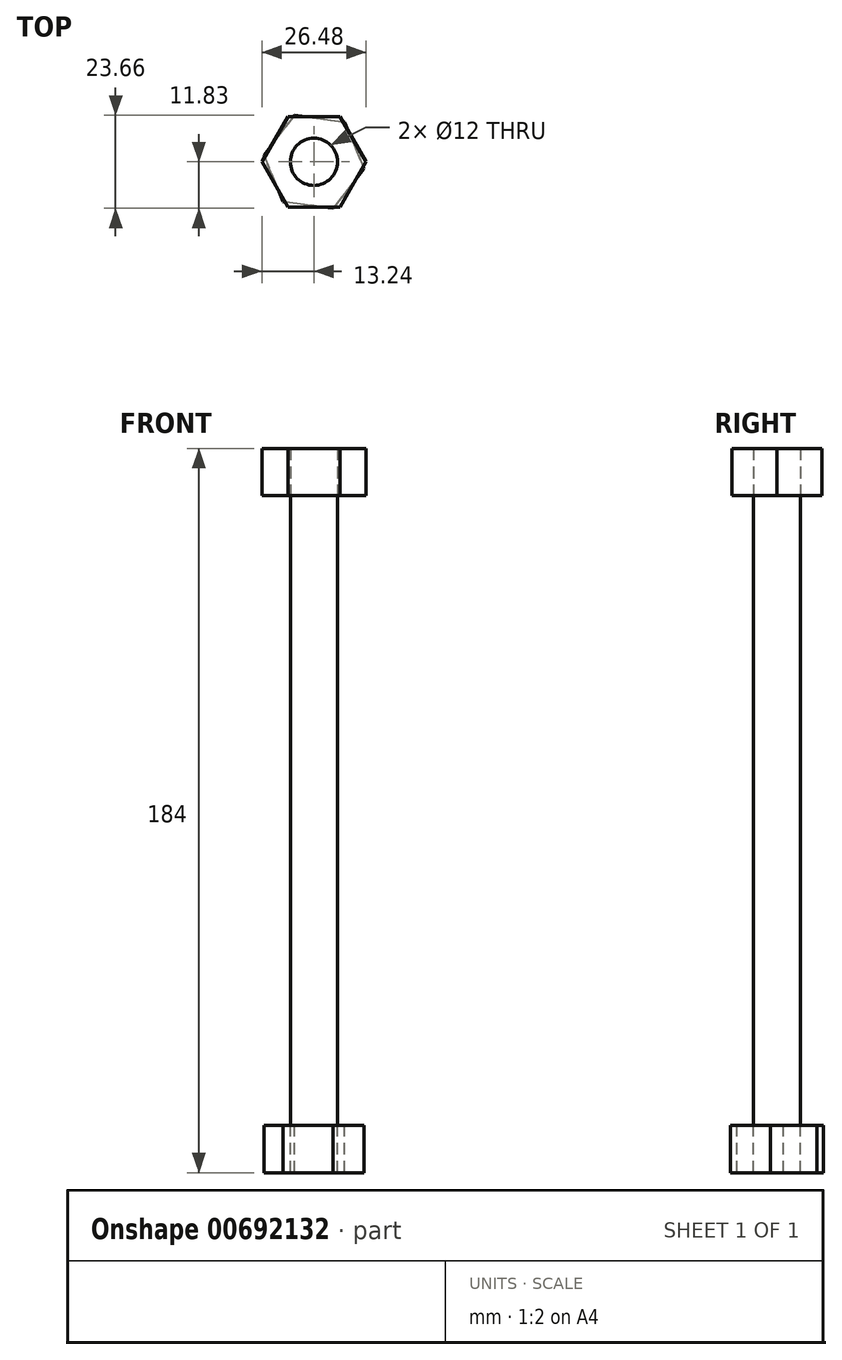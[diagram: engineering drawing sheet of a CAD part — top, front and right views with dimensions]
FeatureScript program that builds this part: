
annotation { "Feature Type Name" : "Feature", "Feature Type Description" : "" }
export const myFeature = defineFeature(function(context is Context, id is Id, definition is map)
    precondition{}
    {
        {
            var Q0;
            Q0=qCreatedBy(makeId("Top.planeOp"),FACE);
            var sketch = newSketch(context, id + "F0", { "sketchPlane" : qUnion([Q0])});
            skCircle(sketch, "E0", {"center": v(0, 0) * mm, "radius": 6 * mm});
            skCircle(sketch, "E1.cCircle", {"center": v(0, 0) * mm, "radius": 11.08 * mm, "construction": true});
            skLineSegment(sketch, "E1.0", {"start": v(-12.68, 1.69) * mm, "end": v(-4.88, 11.83) * mm});
            skLineSegment(sketch, "E1.1", {"start": v(-4.88, 11.83) * mm, "end": v(7.8, 10.14) * mm});
            skLineSegment(sketch, "E1.2", {"start": v(7.8, 10.14) * mm, "end": v(12.68, -1.69) * mm});
            skLineSegment(sketch, "E1.3", {"start": v(12.68, -1.69) * mm, "end": v(4.88, -11.83) * mm});
            skLineSegment(sketch, "E1.4", {"start": v(4.88, -11.83) * mm, "end": v(-7.8, -10.14) * mm});
            skLineSegment(sketch, "E1.5", {"start": v(-7.8, -10.14) * mm, "end": v(-12.68, 1.69) * mm});
            skPoint(sketch, "E1.0.midPoint", {"position": v(-8.78, 6.76) * mm});
            skSolve(sketch);
        }
        {
            var Q0;
            Q0=makeQuery(id+"F0.imprint","IMPRINT",FACE,{"disambiguationData":[TD([[makeQuery(id+"F0.imprint","IMPRINT",EDGE,{"derivedFrom":sQuery(id+"F0.wireOp",EDGE,"E0")}),1.0]])]});
            extrude(context, id + "F1", {"entities" : qUnion([Q0]), "depth" : 160 * mm, "offsetDistance" : 25 * mm});
        }
        {
            var Q0;
            Q0=qSketchRegion(id+"F0",true);
            extrude(context, id + "F2", {"entities" : qUnion([Q0]), "operationType" : NewBodyOperationType.ADD, "oppositeDirection" : true, "depth" : 12 * mm, "offsetDistance" : 25 * mm});
        }
        {
            var Q0;
            Q0=makeQuery(id+"F1.opExtrude","CAP_FACE",FACE,{"disambiguationData":[OSD([sQuery(id+"F0.wireOp",EDGE,"E0")])],"isStart":false});
            var sketch = newSketch(context, id + "F3", { "sketchPlane" : qUnion([Q0])});
            skCircle(sketch, "E2.cCircle", {"center": v(0, 0) * mm, "radius": 11.47 * mm, "construction": true});
            skLineSegment(sketch, "E2.0", {"start": v(6.62, -11.47) * mm, "end": v(-6.62, -11.47) * mm});
            skLineSegment(sketch, "E2.1", {"start": v(-6.62, -11.47) * mm, "end": v(-13.24, 0) * mm});
            skLineSegment(sketch, "E2.2", {"start": v(-13.24, 0) * mm, "end": v(-6.62, 11.47) * mm});
            skLineSegment(sketch, "E2.3", {"start": v(-6.62, 11.47) * mm, "end": v(6.62, 11.47) * mm});
            skLineSegment(sketch, "E2.4", {"start": v(6.62, 11.47) * mm, "end": v(13.24, 0) * mm});
            skLineSegment(sketch, "E2.5", {"start": v(13.24, 0) * mm, "end": v(6.62, -11.47) * mm});
            skPoint(sketch, "E2.0.midPoint", {"position": v(0, -11.47) * mm});
            skSolve(sketch);
        }
        {
            var Q0;
            Q0=makeQuery(id+"F3.imprint","IMPRINT",FACE,{"disambiguationData":[TD([[makeQuery(id+"F3.imprint","IMPRINT",EDGE,{"derivedFrom":sQuery(id+"F3.wireOp",EDGE,"E2.0")}),-1.0]])]});
            extrude(context, id + "F4", {"entities" : qUnion([Q0]), "depth" : 12 * mm, "offsetDistance" : 25 * mm});
        }
    });
